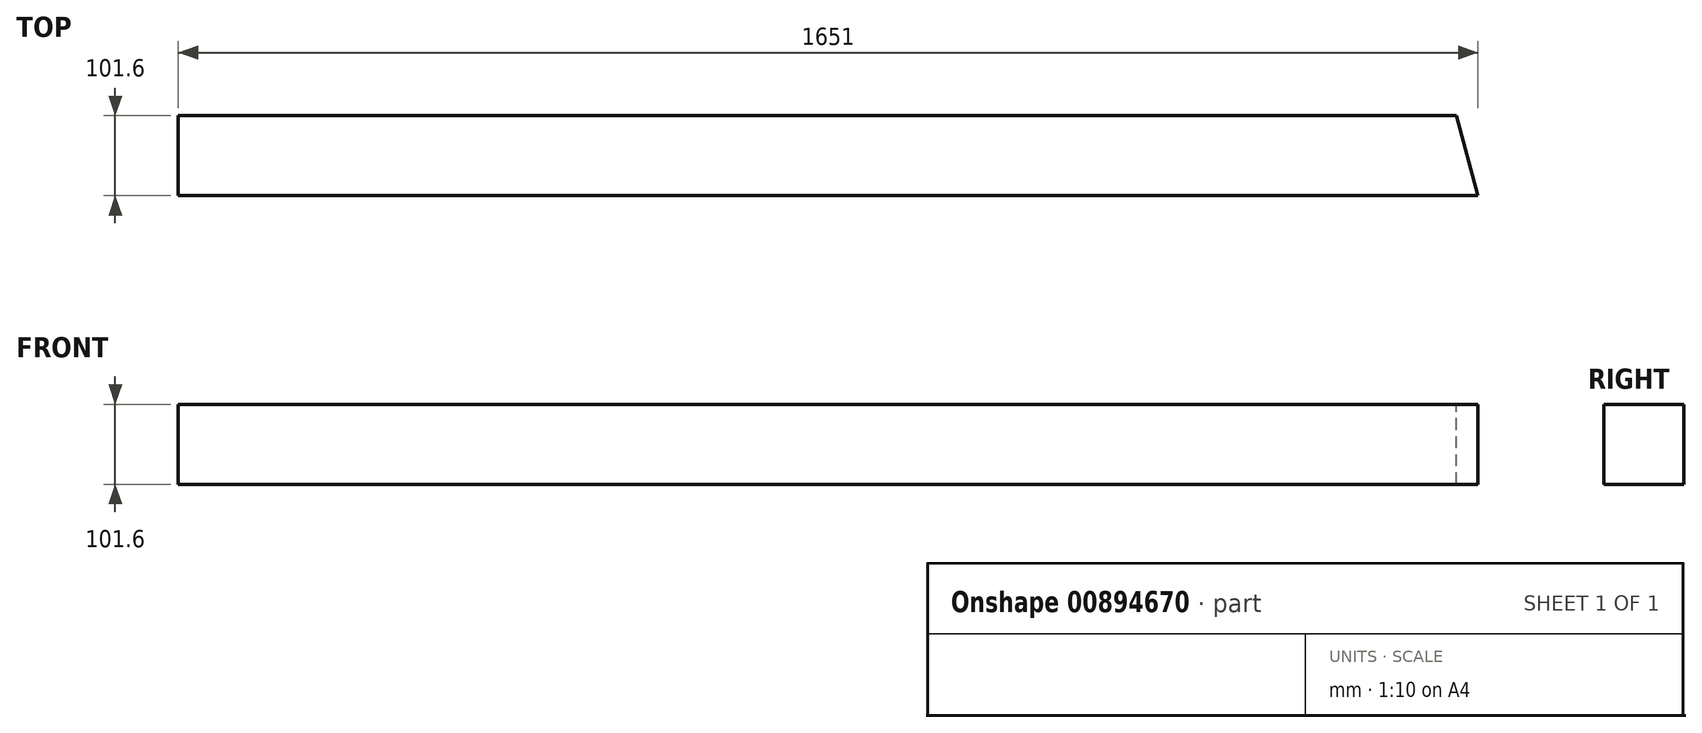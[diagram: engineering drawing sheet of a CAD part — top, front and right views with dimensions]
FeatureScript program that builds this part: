
annotation { "Feature Type Name" : "Feature", "Feature Type Description" : "" }
export const myFeature = defineFeature(function(context is Context, id is Id, definition is map)
    precondition{}
    {
        {
            var Q0;
            Q0=qCreatedBy(makeId("Right.planeOp"),FACE);
            var sketch = newSketch(context, id + "F0", { "sketchPlane" : qUnion([Q0])});
            skLineSegment(sketch, "E0.bottom", {"start": v(0, 0) * mm, "end": v(101.6, 0) * mm});
            skLineSegment(sketch, "E0.top", {"start": v(0, -101.6) * mm, "end": v(101.6, -101.6) * mm});
            skLineSegment(sketch, "E0.left", {"start": v(0, 0) * mm, "end": v(0, -101.6) * mm});
            skLineSegment(sketch, "E0.right", {"start": v(101.6, 0) * mm, "end": v(101.6, -101.6) * mm});
            skSolve(sketch);
        }
        {
            var Q0;
            Q0 = qSketchRegion(id + "F0", true);
            extrude(context, id + "F1", {"entities" : qUnion([Q0]), "depth" : 1651 * mm, "offsetDistance" : 25.4 * mm});
        }
        {
            var Q0;
            Q0=qCreatedBy(makeId("Top.planeOp"),FACE);
            var sketch = newSketch(context, id + "F2", { "sketchPlane" : qUnion([Q0])});
            skLineSegment(sketch, "E1", {"start": v(1623.78, 101.6) * mm, "end": v(1651, 0) * mm});
            skLineSegment(sketch, "E2", {"start": v(1651, 0) * mm, "end": v(1651, 101.6) * mm});
            skLineSegment(sketch, "E3", {"start": v(1651, 101.6) * mm, "end": v(1623.78, 101.6) * mm});
            skSolve(sketch);
        }
        {
            var Q0;
            Q0 = qSketchRegion(id + "F2", true);
            extrude(context, id + "F3", {"entities" : qUnion([Q0]), "operationType" : NewBodyOperationType.REMOVE, "oppositeDirection" : true, "depth" : 127 * mm, "offsetDistance" : 25.4 * mm});
        }
    });
